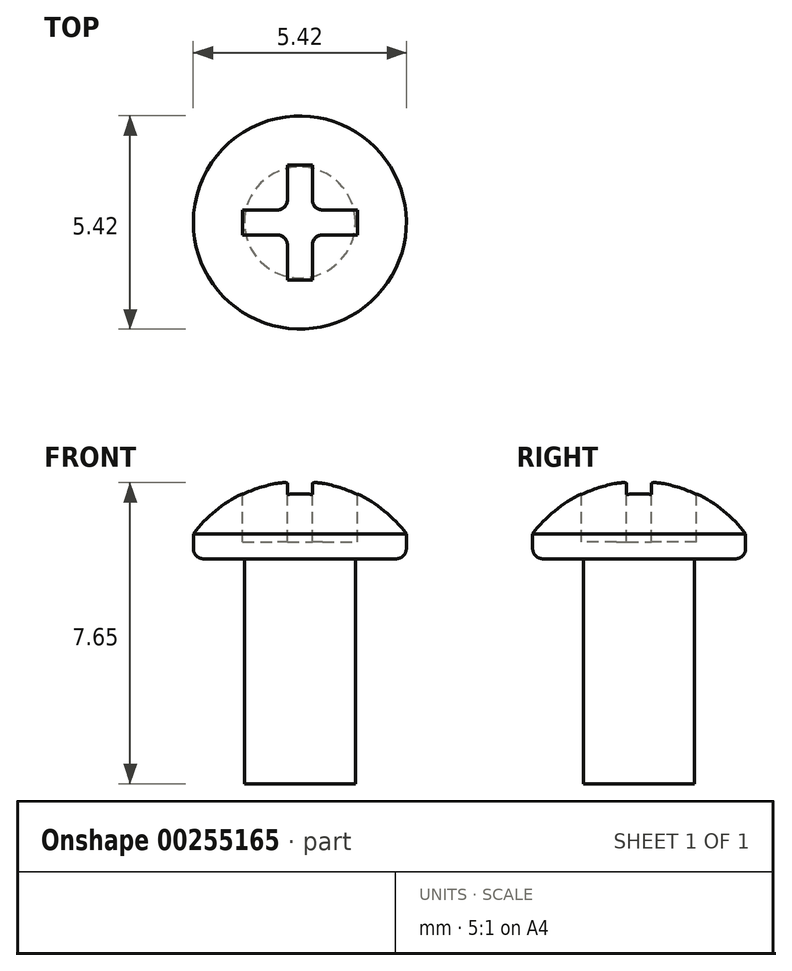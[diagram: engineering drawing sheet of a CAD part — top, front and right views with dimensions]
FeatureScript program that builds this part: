
annotation { "Feature Type Name" : "Feature", "Feature Type Description" : "" }
export const myFeature = defineFeature(function(context is Context, id is Id, definition is map)
    precondition{}
    {
        {
            var Q0;
            Q0=qCreatedBy(makeId("Top.planeOp"),FACE);
            var sketch = newSketch(context, id + "F0", { "sketchPlane" : qUnion([Q0])});
            skCircle(sketch, "E0", {"center": v(0, 0) * mm, "radius": 1.4 * mm});
            skSolve(sketch);
        }
        {
            var Q0;
            Q0 = qSketchRegion(id + "F0", true);
            extrude(context, id + "F1", {"entities" : qUnion([Q0]), "depth" : 5.7 * mm});
        }
        {
            var Q0;
            Q0=qCreatedBy(makeId("Right.planeOp"),FACE);
            var sketch = newSketch(context, id + "F2", { "sketchPlane" : qUnion([Q0])});
            skLineSegment(sketch, "E1", {"start": v(0, 5.72) * mm, "end": v(0, 7.7) * mm});
            skLineSegment(sketch, "E2", {"start": v(-2.7, 5.72) * mm, "end": v(-2.7, 6.35) * mm});
            skArc(sketch, "E3", {"start": v(0, 7.7) * mm, "mid": v(-1.51, 7.34) * mm, "end": v(-2.7, 6.35) * mm});
            skLineSegment(sketch, "E4", {"start": v(0, 5.72) * mm, "end": v(-2.7, 5.72) * mm});
            skSolve(sketch);
        }
        {
            var Q0;
            Q0 = qSketchRegion(id + "F2", true);
            var Q1;
            Q1=sQuery(id+"F2.wireOp",EDGE,"E1");
            revolve(context, id + "F3", {"operationType" : NewBodyOperationType.ADD, "entities" : qUnion([Q0]), "axis" : qUnion([Q1]), "revolveType" : RevolveType.FULL});
        }
        {
            var Q0;
            Q0=qCreatedBy(makeId("Top.planeOp"),FACE);
            cPlane(context, id + "F4", {"entities" : qUnion([Q0]), "cplaneType" : CPlaneType.OFFSET, "offset" : 7.75 * mm, "width" : 152.4 * mm, "height" : 152.4 * mm});
        }
        {
            var Q0;
            Q0=qCreatedBy(id+"F4.planeOp",FACE);
            var sketch = newSketch(context, id + "F5", { "sketchPlane" : qUnion([Q0])});
            skLineSegment(sketch, "E5.bottom", {"start": v(-1.46, -0.32) * mm, "end": v(-0.32, -0.32) * mm});
            skLineSegment(sketch, "E5.top", {"start": v(-1.46, 0.32) * mm, "end": v(-0.32, 0.32) * mm});
            skLineSegment(sketch, "E5.left", {"start": v(-1.46, -0.32) * mm, "end": v(-1.46, 0.32) * mm});
            skLineSegment(sketch, "E5.right", {"start": v(1.46, -0.32) * mm, "end": v(1.46, 0.32) * mm});
            skLineSegment(sketch, "E6.bottom", {"start": v(-0.32, 1.46) * mm, "end": v(0.32, 1.46) * mm});
            skLineSegment(sketch, "E6.top", {"start": v(-0.32, -1.46) * mm, "end": v(0.32, -1.46) * mm});
            skLineSegment(sketch, "E6.left", {"start": v(-0.32, 1.46) * mm, "end": v(-0.32, 0.32) * mm});
            skLineSegment(sketch, "E6.right", {"start": v(0.32, 1.46) * mm, "end": v(0.32, 0.32) * mm});
            skLineSegment(sketch, "E7.trimOffspring", {"start": v(0.32, 0.32) * mm, "end": v(1.46, 0.32) * mm});
            skLineSegment(sketch, "E8.trimOffspring", {"start": v(-0.32, -0.32) * mm, "end": v(-0.32, -1.46) * mm});
            skLineSegment(sketch, "E9.trimOffspring", {"start": v(0.32, -0.32) * mm, "end": v(1.46, -0.32) * mm});
            skLineSegment(sketch, "E10.trimOffspring", {"start": v(0.32, -0.32) * mm, "end": v(0.32, -1.46) * mm});
            skLineSegment(sketch, "E11", {"start": v(0, -1.46) * mm, "end": v(0, 1.46) * mm, "construction": true});
            skLineSegment(sketch, "E12", {"start": v(-1.46, 0) * mm, "end": v(1.46, 0) * mm, "construction": true});
            skSolve(sketch);
        }
        {
            var Q0;
            Q0 = qSketchRegion(id + "F5", true);
            extrude(context, id + "F6", {"entities" : qUnion([Q0]), "operationType" : NewBodyOperationType.REMOVE, "oppositeDirection" : true, "depth" : 1.6 * mm});
        }
        {
            var Q0;
            Q0=makeQuery(id+"F6.boolean.opBoolean","COPY",EDGE,{"derivedFrom":makeQuery(id+"F6.opExtrude","SWEPT_EDGE",EDGE,{"disambiguationData":[OSD([sQuery(id+"F5.wireOp",EDGE,"E5.bottom"),sQuery(id+"F5.wireOp",EDGE,"E8.trimOffspring")])]})});
            var Q1;
            Q1=makeQuery(id+"F6.boolean.opBoolean","COPY",EDGE,{"derivedFrom":makeQuery(id+"F6.opExtrude","SWEPT_EDGE",EDGE,{"disambiguationData":[OSD([sQuery(id+"F5.wireOp",EDGE,"E5.top"),sQuery(id+"F5.wireOp",EDGE,"E6.left")])]})});
            var Q2;
            Q2=makeQuery(id+"F6.boolean.opBoolean","COPY",EDGE,{"derivedFrom":makeQuery(id+"F6.opExtrude","SWEPT_EDGE",EDGE,{"disambiguationData":[OSD([sQuery(id+"F5.wireOp",EDGE,"E6.right"),sQuery(id+"F5.wireOp",EDGE,"E7.trimOffspring")])]})});
            var Q3;
            Q3=makeQuery(id+"F6.boolean.opBoolean","COPY",EDGE,{"derivedFrom":makeQuery(id+"F6.opExtrude","SWEPT_EDGE",EDGE,{"disambiguationData":[OSD([sQuery(id+"F5.wireOp",EDGE,"E9.trimOffspring"),sQuery(id+"F5.wireOp",EDGE,"E10.trimOffspring")])]})});
            fillet(context, id + "F7", {"entities" : qUnion([Q0, Q1, Q2, Q3]), "radius" : 0.25 * mm, "tangentPropagation" : true, "allowEdgeOverflow" : false});
        }
        {
            var Q0;
            Q0=makeQuery(id+"F3.opRevolve","SWEPT_EDGE",EDGE,{"disambiguationData":[OSD([sQuery(id+"F2.wireOp",EDGE,"E2"),sQuery(id+"F2.wireOp",EDGE,"E4")])]});
            fillet(context, id + "F8", {"entities" : qUnion([Q0]), "radius" : 0.25 * mm, "tangentPropagation" : true, "allowEdgeOverflow" : false});
        }
    });
